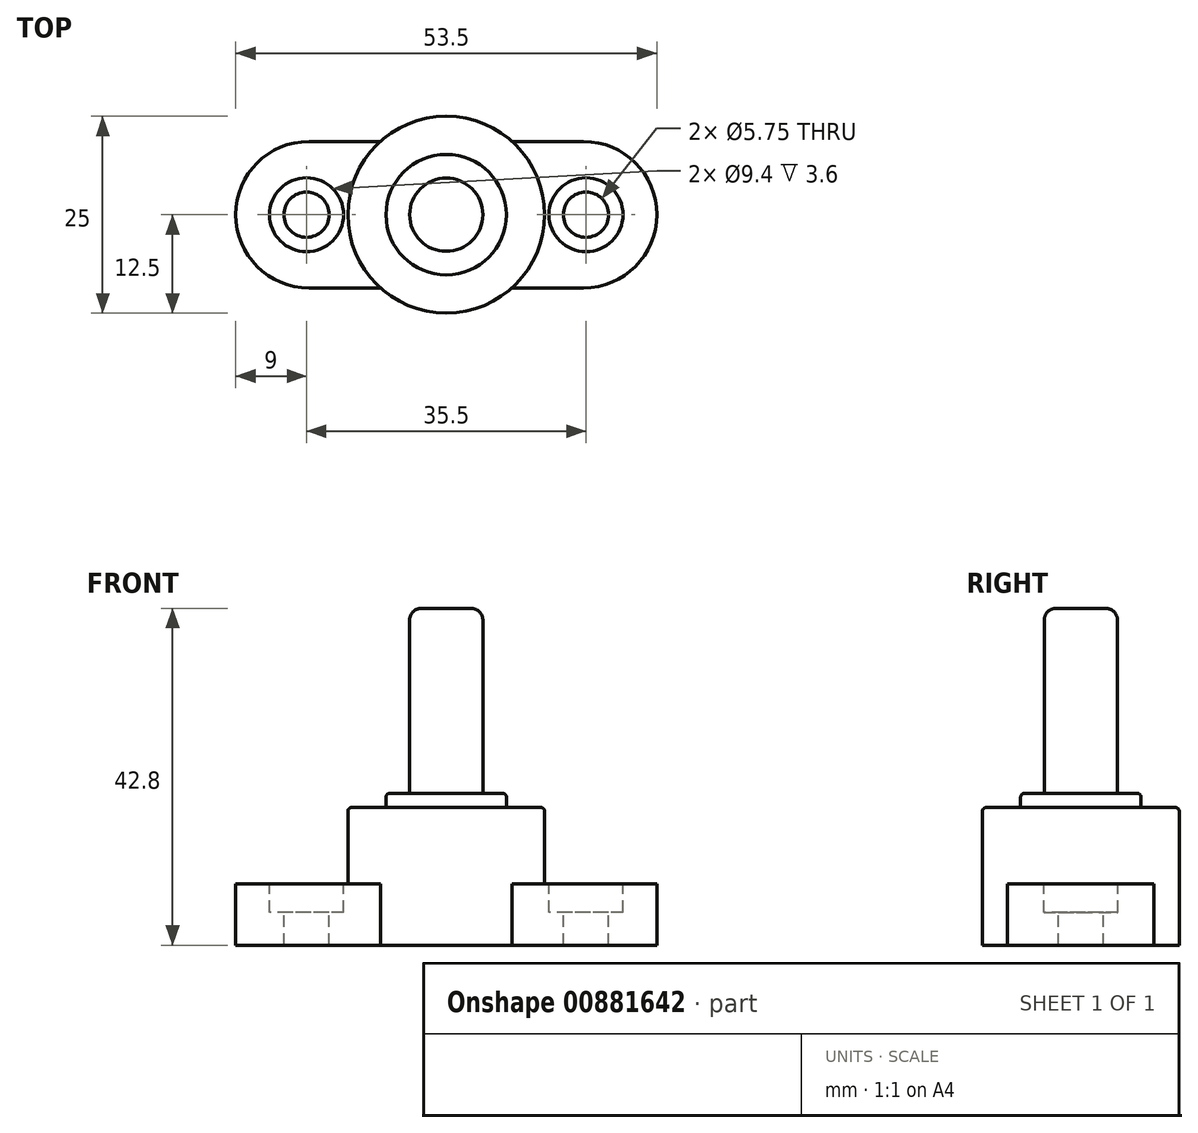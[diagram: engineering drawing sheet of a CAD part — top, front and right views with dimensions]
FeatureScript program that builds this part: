
annotation { "Feature Type Name" : "Feature", "Feature Type Description" : "" }
export const myFeature = defineFeature(function(context is Context, id is Id, definition is map)
    precondition{}
    {
        {
            var Q0;
            Q0=qCreatedBy(makeId("Top.planeOp"),FACE);
            var sketch = newSketch(context, id + "F0", { "sketchPlane" : qUnion([Q0])});
            skLineSegment(sketch, "E0.bottom", {"start": v(26.75, 9.3) * mm, "end": v(-26.75, 9.3) * mm});
            skLineSegment(sketch, "E0.top", {"start": v(26.75, -9.3) * mm, "end": v(-26.75, -9.3) * mm});
            skLineSegment(sketch, "E0.left", {"start": v(26.75, 9.3) * mm, "end": v(26.75, -9.3) * mm});
            skLineSegment(sketch, "E0.right", {"start": v(-26.75, 9.3) * mm, "end": v(-26.75, -9.3) * mm});
            skPoint(sketch, "E0.middle", {"position": v(0, 0) * mm});
            skCircle(sketch, "E1", {"center": v(0, 0) * mm, "radius": 12.5 * mm});
            skCircle(sketch, "E2", {"center": v(0, 0) * mm, "radius": 7.65 * mm});
            skCircle(sketch, "E3", {"center": v(0, 0) * mm, "radius": 4.65 * mm});
            skLineSegment(sketch, "E4", {"start": v(-26.75, 0) * mm, "end": v(26.75, 0) * mm, "construction": true});
            skPoint(sketch, "E5", {"position": v(-17.75, 0) * mm});
            skLineSegment(sketch, "E6", {"start": v(0, 9.3) * mm, "end": v(0, -9.3) * mm, "construction": true});
            skPoint(sketch, "E7.MirrorP", {"position": v(17.75, 0) * mm});
            skArc(sketch, "E8", {"start": v(17.45, 9.3) * mm, "mid": v(8.15, 0) * mm, "end": v(17.45, -9.3) * mm, "construction": true});
            skArc(sketch, "E9", {"start": v(17.45, -9.3) * mm, "mid": v(26.75, 0) * mm, "end": v(17.45, 9.3) * mm});
            skArc(sketch, "E10.MirrorCS", {"start": v(-17.45, -9.3) * mm, "mid": v(-26.75, 0) * mm, "end": v(-17.45, 9.3) * mm});
            skSolve(sketch);
        }
        {
            var Q0;
            {var subQ0=sQuery(id+"F0.wireOp",EDGE,"E10.MirrorCS");var subQ5=sQuery(id+"F0.wireOp",EDGE,"E0.bottom");var subQ8=makeQuery(id+"F0.imprint","INTERSECT",VERTEX,{"derivedFrom":[subQ5,subQ0]});Q0=makeQuery(id+"F0.imprint","IMPRINT",FACE,{"disambiguationData":[TD([[makeQuery(id+"F0.imprint","IMPRINT",EDGE,{"disambiguationData":[TD([[subQ8,1.0]])],"derivedFrom":subQ5}),1.0]])]});}
            var Q1;
            Q1=makeQuery(id+"F0.imprint","IMPRINT",FACE,{"disambiguationData":[TD([[makeQuery(id+"F0.imprint","IMPRINT",EDGE,{"derivedFrom":sQuery(id+"F0.wireOp",EDGE,"E2")}),-1.0]])]});
            var Q2;
            Q2=makeQuery(id+"F0.imprint","IMPRINT",FACE,{"disambiguationData":[TD([[makeQuery(id+"F0.imprint","IMPRINT",EDGE,{"derivedFrom":sQuery(id+"F0.wireOp",EDGE,"E2")}),1.0]])]});
            var Q3;
            Q3=makeQuery(id+"F0.imprint","IMPRINT",FACE,{"disambiguationData":[TD([[makeQuery(id+"F0.imprint","IMPRINT",EDGE,{"derivedFrom":sQuery(id+"F0.wireOp",EDGE,"E3")}),1.0]])]});
            var Q4;
            {var subQ0=sQuery(id+"F0.wireOp",EDGE,"E9");var subQ5=sQuery(id+"F0.wireOp",EDGE,"E0.bottom");var subQ8=makeQuery(id+"F0.imprint","INTERSECT",VERTEX,{"derivedFrom":[subQ5,subQ0]});Q4=makeQuery(id+"F0.imprint","IMPRINT",FACE,{"disambiguationData":[TD([[makeQuery(id+"F0.imprint","IMPRINT",EDGE,{"disambiguationData":[TD([[subQ8,-1.0]])],"derivedFrom":subQ5}),1.0]])]});}
            var Q5;
            {var subQ0=sQuery(id+"F0.wireOp",EDGE,"E1");var subQ1=sQuery(id+"F0.wireOp",EDGE,"E0.bottom");var subQ2=makeQuery(id+"F0.imprint","INTERSECT",VERTEX,{"disambiguationData":[OD(0.0)],"derivedFrom":[subQ1,subQ0]});Q5=makeQuery(id+"F0.imprint","IMPRINT",FACE,{"disambiguationData":[TD([[makeQuery(id+"F0.imprint","IMPRINT",EDGE,{"disambiguationData":[TD([[subQ2,-1.0]])],"derivedFrom":subQ1}),-1.0]])]});}
            var Q6;
            {var subQ0=sQuery(id+"F0.wireOp",EDGE,"E1");var subQ1=sQuery(id+"F0.wireOp",EDGE,"E0.top");var subQ2=makeQuery(id+"F0.imprint","INTERSECT",VERTEX,{"disambiguationData":[OD(0.0)],"derivedFrom":[subQ1,subQ0]});Q6=makeQuery(id+"F0.imprint","IMPRINT",FACE,{"disambiguationData":[TD([[makeQuery(id+"F0.imprint","IMPRINT",EDGE,{"disambiguationData":[TD([[subQ2,-1.0]])],"derivedFrom":subQ1}),1.0]])]});}
            extrude(context, id + "F1", {"entities" : qUnion([Q0, Q1, Q2, Q3, Q4, Q5, Q6]), "oppositeDirection" : true, "depth" : 7.8 * mm, "offsetDistance" : 25 * mm});
        }
        {
            var Q0;
            {var subQ0=sQuery(id+"F0.wireOp",EDGE,"E1");var subQ1=sQuery(id+"F0.wireOp",EDGE,"E0.bottom");var subQ2=makeQuery(id+"F0.imprint","INTERSECT",VERTEX,{"disambiguationData":[OD(0.0)],"derivedFrom":[subQ1,subQ0]});Q0=makeQuery(id+"F0.imprint","IMPRINT",FACE,{"disambiguationData":[TD([[makeQuery(id+"F0.imprint","IMPRINT",EDGE,{"disambiguationData":[TD([[subQ2,-1.0]])],"derivedFrom":subQ1}),-1.0]])]});}
            var Q1;
            {var subQ0=sQuery(id+"F0.wireOp",EDGE,"E1");var subQ1=sQuery(id+"F0.wireOp",EDGE,"E0.top");var subQ2=makeQuery(id+"F0.imprint","INTERSECT",VERTEX,{"disambiguationData":[OD(0.0)],"derivedFrom":[subQ1,subQ0]});Q1=makeQuery(id+"F0.imprint","IMPRINT",FACE,{"disambiguationData":[TD([[makeQuery(id+"F0.imprint","IMPRINT",EDGE,{"disambiguationData":[TD([[subQ2,-1.0]])],"derivedFrom":subQ1}),1.0]])]});}
            var Q2;
            Q2=makeQuery(id+"F0.imprint","IMPRINT",FACE,{"disambiguationData":[TD([[makeQuery(id+"F0.imprint","IMPRINT",EDGE,{"derivedFrom":sQuery(id+"F0.wireOp",EDGE,"E2")}),-1.0]])]});
            var Q3;
            Q3=makeQuery(id+"F0.imprint","IMPRINT",FACE,{"disambiguationData":[TD([[makeQuery(id+"F0.imprint","IMPRINT",EDGE,{"derivedFrom":sQuery(id+"F0.wireOp",EDGE,"E2")}),1.0]])]});
            var Q4;
            Q4=makeQuery(id+"F0.imprint","IMPRINT",FACE,{"disambiguationData":[TD([[makeQuery(id+"F0.imprint","IMPRINT",EDGE,{"derivedFrom":sQuery(id+"F0.wireOp",EDGE,"E3")}),1.0]])]});
            extrude(context, id + "F2", {"entities" : qUnion([Q0, Q1, Q2, Q3, Q4]), "operationType" : NewBodyOperationType.ADD, "depth" : 9.7 * mm, "offsetDistance" : 25 * mm});
        }
        {
            var Q0;
            Q0=makeQuery(id+"F0.imprint","IMPRINT",FACE,{"disambiguationData":[TD([[makeQuery(id+"F0.imprint","IMPRINT",EDGE,{"derivedFrom":sQuery(id+"F0.wireOp",EDGE,"E2")}),1.0]])]});
            var Q1;
            Q1=makeQuery(id+"F0.imprint","IMPRINT",FACE,{"disambiguationData":[TD([[makeQuery(id+"F0.imprint","IMPRINT",EDGE,{"derivedFrom":sQuery(id+"F0.wireOp",EDGE,"E3")}),1.0]])]});
            extrude(context, id + "F3", {"entities" : qUnion([Q0, Q1]), "operationType" : NewBodyOperationType.ADD, "depth" : 11.5 * mm, "offsetDistance" : 25 * mm});
        }
        {
            var Q0;
            Q0=makeQuery(id+"F0.imprint","IMPRINT",FACE,{"disambiguationData":[TD([[makeQuery(id+"F0.imprint","IMPRINT",EDGE,{"derivedFrom":sQuery(id+"F0.wireOp",EDGE,"E3")}),1.0]])]});
            extrude(context, id + "F4", {"entities" : qUnion([Q0]), "operationType" : NewBodyOperationType.ADD, "depth" : 35 * mm, "offsetDistance" : 25 * mm});
        }
        {
            var Q0;
            Q0=sQuery(id+"F0.wireOp",VERTEX,"E5");
            var Q1;
            Q1=sQuery(id+"F0.wireOp",VERTEX,"E7.MirrorP");
            var Q2;
            Q2=makeQuery(id+"F1.opExtrude","SWEPT_BODY",BODY,{"disambiguationData":[OSD([sQuery(id+"F0.wireOp",EDGE,"E0.bottom"),sQuery(id+"F0.wireOp",EDGE,"E0.top"),sQuery(id+"F0.wireOp",EDGE,"E1"),sQuery(id+"F0.wireOp",EDGE,"E9"),sQuery(id+"F0.wireOp",EDGE,"E10.MirrorCS")])]});
            hole(context, id + "F5", {"style" : HoleStyle.C_BORE, "endStyle" : HoleEndStyle.THROUGH, "holeDiameter" : 5.75 * mm, "cBoreDiameter" : 9.4 * mm, "cBoreDepth" : 3.6 * mm, "majorDiameter" : 5 * mm, "isTappedThrough" : true, "tappedDepth" : 12 * mm, "tapClearance" : 3, "startFromSketch" : true, "locations" : qUnion([Q0, Q1]), "scope" : qUnion([Q2])});
        }
        {
            var Q0;
            Q0=makeQuery(id+"F2.opExtrude","CAP_EDGE",EDGE,{"disambiguationData":[OSD([sQuery(id+"F0.wireOp",EDGE,"E1")])],"isStart":false});
            var Q1;
            Q1=makeQuery(id+"F3.opExtrude","CAP_EDGE",EDGE,{"disambiguationData":[OSD([sQuery(id+"F0.wireOp",EDGE,"E2")])],"isStart":false});
            fillet(context, id + "F6", {"entities" : qUnion([Q0, Q1]), "radius" : .5 * mm, "tangentPropagation" : true, "allowEdgeOverflow" : false});
        }
        {
            var Q0;
            Q0=makeQuery(id+"F4.opExtrude","CAP_FACE",FACE,{"disambiguationData":[OSD([sQuery(id+"F0.wireOp",EDGE,"E3")])],"isStart":false});
            fillet(context, id + "F7", {"entities" : qUnion([Q0]), "radius" : 1.5 * mm, "tangentPropagation" : true, "allowEdgeOverflow" : false});
        }
    });
